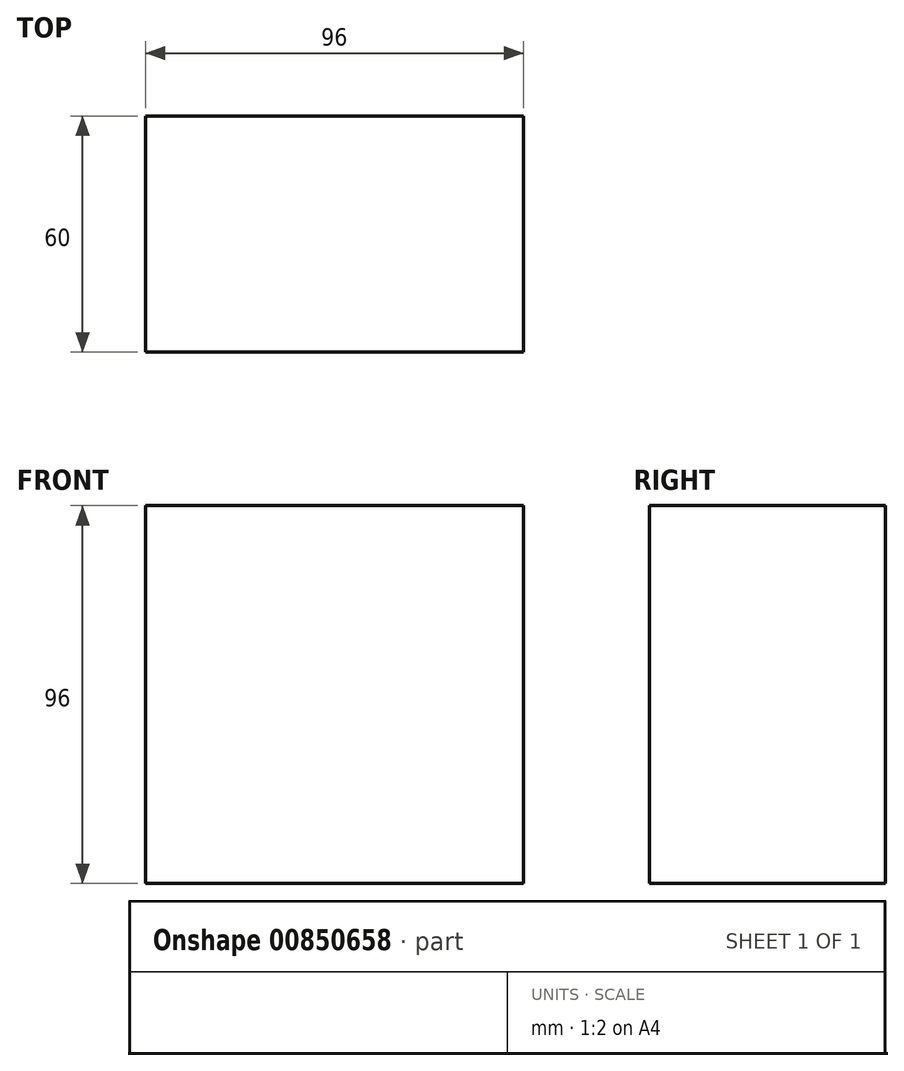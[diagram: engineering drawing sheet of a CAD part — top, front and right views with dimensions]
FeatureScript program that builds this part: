
annotation { "Feature Type Name" : "Feature", "Feature Type Description" : "" }
export const myFeature = defineFeature(function(context is Context, id is Id, definition is map)
    precondition{}
    {
        {
            var Q0;
            Q0=qCreatedBy(makeId("Front.planeOp"),FACE);
            var sketch = newSketch(context, id + "F0", { "sketchPlane" : qUnion([Q0])});
            skLineSegment(sketch, "E0.bottom", {"start": v(-72.02, 52.95) * mm, "end": v(23.98, 52.95) * mm});
            skLineSegment(sketch, "E0.top", {"start": v(-72.02, -43.05) * mm, "end": v(23.98, -43.05) * mm});
            skLineSegment(sketch, "E0.left", {"start": v(-72.02, 52.95) * mm, "end": v(-72.02, -43.05) * mm});
            skLineSegment(sketch, "E0.right", {"start": v(23.98, 52.95) * mm, "end": v(23.98, -43.05) * mm});
            skSolve(sketch);
        }
        {
            var Q0;
            Q0 = qSketchRegion(id + "F0", true);
            extrude(context, id + "F1", {"entities" : qUnion([Q0]), "depth" : 60 * mm, "offsetDistance" : 25 * mm});
        }
    });
